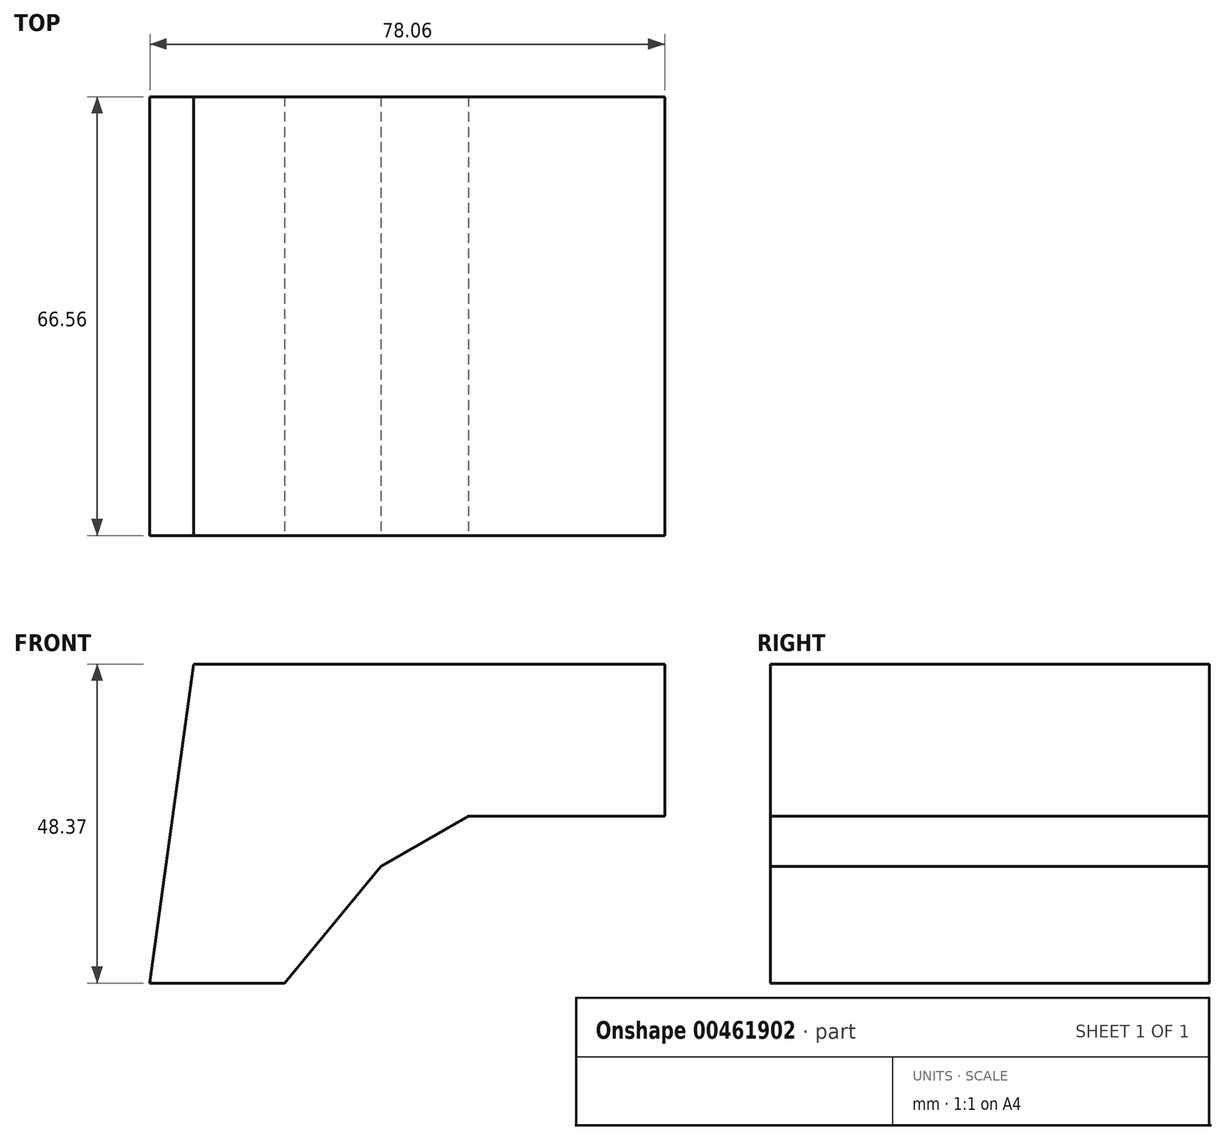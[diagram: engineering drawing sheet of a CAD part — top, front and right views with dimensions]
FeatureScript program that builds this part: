
annotation { "Feature Type Name" : "Feature", "Feature Type Description" : "" }
export const myFeature = defineFeature(function(context is Context, id is Id, definition is map)
    precondition{}
    {
        {
            var Q0;
            Q0=qCreatedBy(makeId("Front.planeOp"),FACE);
            var sketch = newSketch(context, id + "F0", { "sketchPlane" : qUnion([Q0])});
            skLineSegment(sketch, "E0", {"start": v(-35.05, -35.74) * mm, "end": v(-14.66, -35.74) * mm});
            skLineSegment(sketch, "E1", {"start": v(-14.66, -35.74) * mm, "end": v(0, -18.04) * mm});
            skLineSegment(sketch, "E2", {"start": v(0, -18.04) * mm, "end": v(13.25, -10.44) * mm});
            skLineSegment(sketch, "E3", {"start": v(13.25, -10.44) * mm, "end": v(43, -10.44) * mm});
            skLineSegment(sketch, "E4", {"start": v(43, -10.44) * mm, "end": v(43, 12.63) * mm});
            skLineSegment(sketch, "E5", {"start": v(43, 12.63) * mm, "end": v(-11.01, 12.63) * mm});
            skLineSegment(sketch, "E6", {"start": v(-11.01, 12.63) * mm, "end": v(-28.42, 12.63) * mm});
            skLineSegment(sketch, "E7", {"start": v(-28.42, 12.63) * mm, "end": v(-35.05, -35.74) * mm});
            skSolve(sketch);
        }
        {
            var Q0;
            Q0 = qSketchRegion(id + "F0", true);
            extrude(context, id + "F1", {"entities" : qUnion([Q0]), "oppositeDirection" : true, "depth" : 66.56 * mm});
        }
        {
            var Q0;
            Q0=qCreatedBy(makeId("Front.planeOp"),FACE);
            var sketch = newSketch(context, id + "F2", { "sketchPlane" : qUnion([Q0])});
            skLineSegment(sketch, "E8", {"start": v(41.95, -9.06) * mm, "end": v(13.7, -9.06) * mm});
            skLineSegment(sketch, "E9", {"start": v(13.7, -9.06) * mm, "end": v(0, -16.5) * mm});
            skLineSegment(sketch, "E10", {"start": v(-11.92, -36.6) * mm, "end": v(-11.92, -36.6) * mm});
            skLineSegment(sketch, "E11", {"start": v(-11.92, -36.6) * mm, "end": v(0, -16.5) * mm});
            skSolve(sketch);
        }
        {
            var Q0;
            Q0=sQuery(id+"F2.wireOp",EDGE,"E11");
            var Q1;
            Q1=sQuery(id+"F2.wireOp",EDGE,"E9");
            var Q2;
            Q2=sQuery(id+"F2.wireOp",EDGE,"E8");
            extrude(context, id + "F3", {"bodyType" : ToolBodyType.SURFACE, "surfaceEntities" : qUnion([Q0, Q1, Q2]), "depth" : 25.4 * mm});
        }
    });
